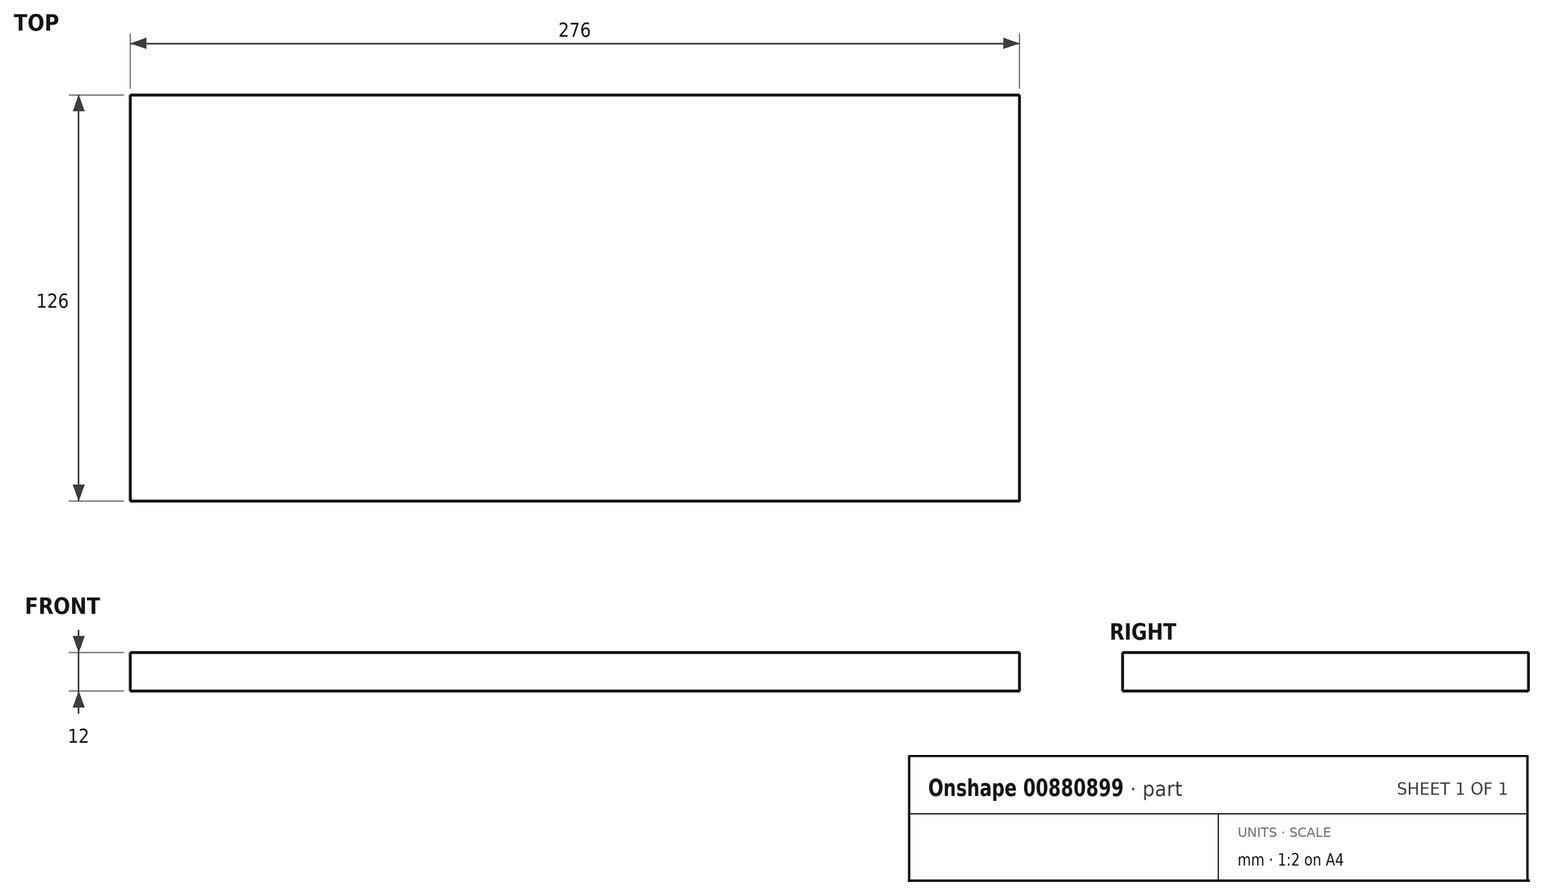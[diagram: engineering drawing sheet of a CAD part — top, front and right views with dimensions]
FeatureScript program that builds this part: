
annotation { "Feature Type Name" : "Feature", "Feature Type Description" : "" }
export const myFeature = defineFeature(function(context is Context, id is Id, definition is map)
    precondition{}
    {
        {
            var Q0;
            Q0=qCreatedBy(makeId("Top.planeOp"),FACE);
            var sketch = newSketch(context, id + "F0", { "sketchPlane" : qUnion([Q0])});
            skLineSegment(sketch, "E0.bottom", {"start": v(-138, -63) * mm, "end": v(138, -63) * mm});
            skLineSegment(sketch, "E0.top", {"start": v(-138, 63) * mm, "end": v(138, 63) * mm});
            skLineSegment(sketch, "E0.left", {"start": v(-138, -63) * mm, "end": v(-138, 63) * mm});
            skLineSegment(sketch, "E0.right", {"start": v(138, -63) * mm, "end": v(138, 63) * mm});
            skPoint(sketch, "E0.middle", {"position": v(0, 0) * mm});
            skSolve(sketch);
        }
        {
            var Q0;
            Q0=makeQuery(id+"F0.imprint","IMPRINT",FACE,{"disambiguationData":[TD([[makeQuery(id+"F0.imprint","IMPRINT",EDGE,{"derivedFrom":sQuery(id+"F0.wireOp",EDGE,"E0.bottom")}),1.0]])]});
            extrude(context, id + "F1", {"entities" : qUnion([Q0]), "depth" : 12 * mm, "offsetDistance" : 25 * mm});
        }
    });
